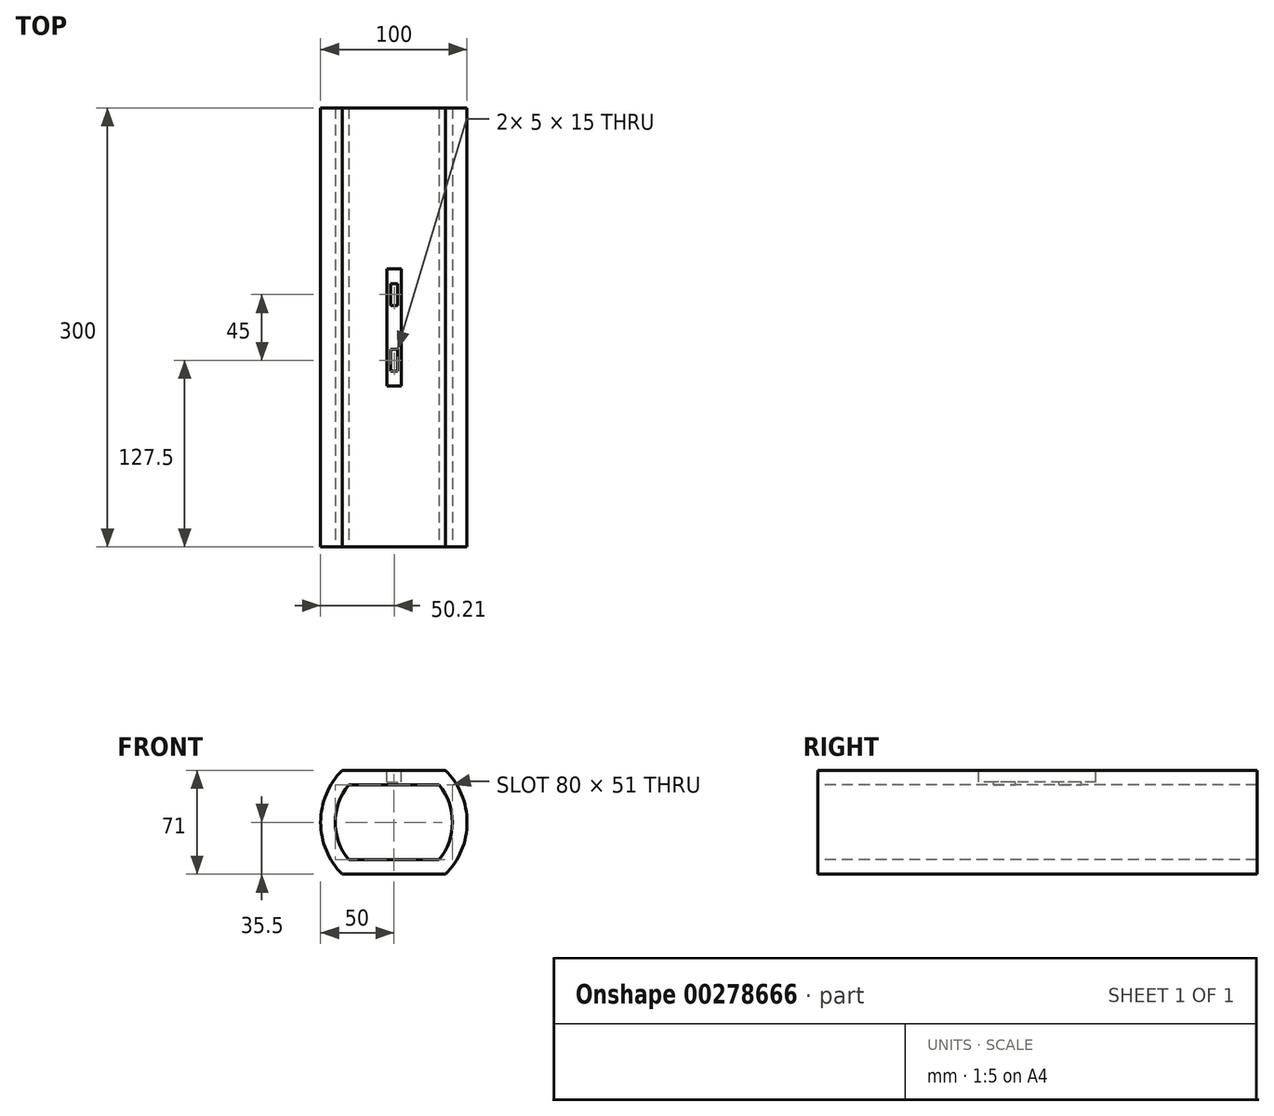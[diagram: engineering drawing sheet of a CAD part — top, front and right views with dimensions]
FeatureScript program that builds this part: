
annotation { "Feature Type Name" : "Feature", "Feature Type Description" : "" }
export const myFeature = defineFeature(function(context is Context, id is Id, definition is map)
    precondition{}
    {
        {
            var Q0;
            Q0=qCreatedBy(makeId("Front.planeOp"),FACE);
            var sketch = newSketch(context, id + "F0", { "sketchPlane" : qUnion([Q0])});
            skArc(sketch, "E0", {"start": v(-35.21, 35.5) * mm, "mid": v(-50, 0) * mm, "end": v(-35.21, -35.5) * mm});
            skLineSegment(sketch, "E1", {"start": v(-35.21, 35.5) * mm, "end": v(35.21, 35.5) * mm});
            skLineSegment(sketch, "E2", {"start": v(-35.21, -35.5) * mm, "end": v(35.21, -35.5) * mm});
            skArc(sketch, "E3.trimOffspring", {"start": v(35.21, -35.5) * mm, "mid": v(50, 0) * mm, "end": v(35.21, 35.5) * mm});
            skSolve(sketch);
        }
        {
            var Q0;
            Q0=qSketchRegion(id+"F0",true);
            extrude(context, id + "F1", {"entities" : qUnion([Q0]), "depth" : 300 * mm});
        }
        {
            var Q0;
            Q0=makeQuery(id+"F1.opExtrude","CAP_FACE",FACE,{"disambiguationData":[OSD([sQuery(id+"F0.wireOp",EDGE,"E0"),sQuery(id+"F0.wireOp",EDGE,"E1"),sQuery(id+"F0.wireOp",EDGE,"E2"),sQuery(id+"F0.wireOp",EDGE,"E3.trimOffspring")])],"isStart":false});
            var sketch = newSketch(context, id + "F2", { "sketchPlane" : qUnion([Q0])});
            skArc(sketch, "E4", {"start": v(-30.82, 25.5) * mm, "mid": v(-40, 0) * mm, "end": v(-30.82, -25.5) * mm});
            skLineSegment(sketch, "E5", {"start": v(-30.82, 25.5) * mm, "end": v(30.82, 25.5) * mm});
            skLineSegment(sketch, "E6", {"start": v(-30.82, -25.5) * mm, "end": v(30.82, -25.5) * mm});
            skArc(sketch, "E7.trimOffspring", {"start": v(30.82, -25.5) * mm, "mid": v(40, 0) * mm, "end": v(30.82, 25.5) * mm});
            skSolve(sketch);
        }
        {
            var Q0;
            Q0=qSketchRegion(id+"F2",true);
            extrude(context, id + "F3", {"entities" : qUnion([Q0]), "operationType" : NewBodyOperationType.REMOVE, "oppositeDirection" : true, "depth" : 300 * mm});
        }
        {
            var Q0;
            Q0=makeQuery(id+"F1.opExtrude","SWEPT_FACE",FACE,{"disambiguationData":[OSD([sQuery(id+"F0.wireOp",EDGE,"E1")])]});
            var sketch = newSketch(context, id + "F4", { "sketchPlane" : qUnion([Q0])});
            skLineSegment(sketch, "E8.bottom", {"start": v(-4.79, -110) * mm, "end": v(5.21, -110) * mm});
            skLineSegment(sketch, "E8.top", {"start": v(-4.79, -190) * mm, "end": v(5.21, -190) * mm});
            skLineSegment(sketch, "E8.left", {"start": v(-4.79, -110) * mm, "end": v(-4.79, -190) * mm});
            skLineSegment(sketch, "E8.right", {"start": v(5.21, -110) * mm, "end": v(5.21, -190) * mm});
            skSolve(sketch);
        }
        {
            var Q0;
            Q0=qSketchRegion(id+"F4",true);
            extrude(context, id + "F5", {"entities" : qUnion([Q0]), "operationType" : NewBodyOperationType.REMOVE, "oppositeDirection" : true, "depth" : 8 * mm});
        }
        {
            var Q0;
            Q0=makeQuery(id+"F5.boolean.opBoolean","COPY",FACE,{"derivedFrom":makeQuery(id+"F5.opExtrude","CAP_FACE",FACE,{"disambiguationData":[OSD([sQuery(id+"F4.wireOp",EDGE,"E8.bottom"),sQuery(id+"F4.wireOp",EDGE,"E8.top"),sQuery(id+"F4.wireOp",EDGE,"E8.left"),sQuery(id+"F4.wireOp",EDGE,"E8.right")])],"isStart":false})});
            var sketch = newSketch(context, id + "F6", { "sketchPlane" : qUnion([Q0])});
            skLineSegment(sketch, "E9.bottom", {"start": v(-2.29, -120) * mm, "end": v(2.71, -120) * mm});
            skLineSegment(sketch, "E9.top", {"start": v(-2.29, -135) * mm, "end": v(2.71, -135) * mm});
            skLineSegment(sketch, "E9.left", {"start": v(-2.29, -120) * mm, "end": v(-2.29, -135) * mm});
            skLineSegment(sketch, "E9.right", {"start": v(2.71, -120) * mm, "end": v(2.71, -135) * mm});
            skLineSegment(sketch, "E10.bottom", {"start": v(-2.29, -165) * mm, "end": v(2.71, -165) * mm});
            skLineSegment(sketch, "E10.top", {"start": v(-2.29, -180) * mm, "end": v(2.71, -180) * mm});
            skLineSegment(sketch, "E10.left", {"start": v(-2.29, -165) * mm, "end": v(-2.29, -180) * mm});
            skLineSegment(sketch, "E10.right", {"start": v(2.71, -165) * mm, "end": v(2.71, -180) * mm});
            skSolve(sketch);
        }
        {
            var Q0;
            Q0=qSketchRegion(id+"F6",true);
            extrude(context, id + "F7", {"entities" : qUnion([Q0]), "operationType" : NewBodyOperationType.REMOVE, "oppositeDirection" : true, "depth" : 5 * mm});
        }
    });
